# Revit family: Shower-Shower_Package-KOHLER-Bancroft-K-22179_1
name_source: partatom
category: Plumbing Fixtures
revit_build: Autodesk Revit 2015 (Build: 20140606_1530(x64)
units: mm (PartAtom-declared; Revit-internal decimal feet)

## types (6) — shared parameters
ADA Compliant = Yes
Assembly Code = D2010700
CW Connection = No
Cold Water Inlet = Cold Water Inlet
Date Modified = 11/21/2019
Default Elevation = 36"
Drain Included = No
HW Connection = Yes
Handle Clearance = 3 3/16"
Height = 28"
Hot Water Inlet = Tempered Water Inlet
Length = 11 1/8"
Manufacturer = KOHLER Co.
MasterFormat 1995 = 15410
MasterFormat 2004 = 22.41.23
Material = Brass Construction
Panel Thickness = 0"
Pressure = 45.00 psi
Product Documentation Link = https://www.us.kohler.com
Product Name = Bancroft
Product Page URL = http://www.us.kohler.com
URL = https://www.us.kohler.com
Vent Connection = No
Waste Connection = No
Waste Water Outlet = Waste Water Outlet
Width = 12"

## per-type parameters (varying)
| type | Description | Finish | Flow Rate | Model | Type | WaterSense Certified |
| 2.5 GPM, CP-Polished Chrome | Essentials performance showering package, 2.5 gpm | Kohler-Metal-CP-Polished_Chrome | 3 GPM | K-22179-CP | 1 | No |
| 2.5 GPM, BN-Vibrant Brushed Nickel | Essentials performance showering package, 2.5 gpm | Kohler-Metal-BN-Vibrant_Brushed_Nickel | 3 GPM | K-22179-BN | 2 | No |
| 2.5 GPM, 2BZ-Oil-Rubbed Bronze | Essentials performance showering package, 2.5 gpm | Kohler-Metal-2BZ-Oil_Rubbed_Bronze | 3 GPM | K-22179-2BZ | 3 | No |
| 1.75 GPM, CP-Polished Chrome | Essentials showering package, 1.75 gpm | Kohler-Metal-CP-Polished_Chrome | 2 GPM | K-22179-G-CP | 4 | Yes |
| 1.75 GPM, BN-Vibrant Brushed Nickel | Essentials showering package, 1.75 gpm | Kohler-Metal-BN-Vibrant_Brushed_Nickel | 2 GPM | K-22179-G-BN | 5 | Yes |
| 1.75 GPM, 2BZ-Oil-Rubbed Bronze | Essentials showering package, 1.75 gpm | Kohler-Metal-2BZ-Oil_Rubbed_Bronze | 2 GPM | K-22179-G-2BZ | 6 | Yes |

## geometry (parser evidence)
native form markers: Sweep x11
no freeform markers — native parametric forms only
